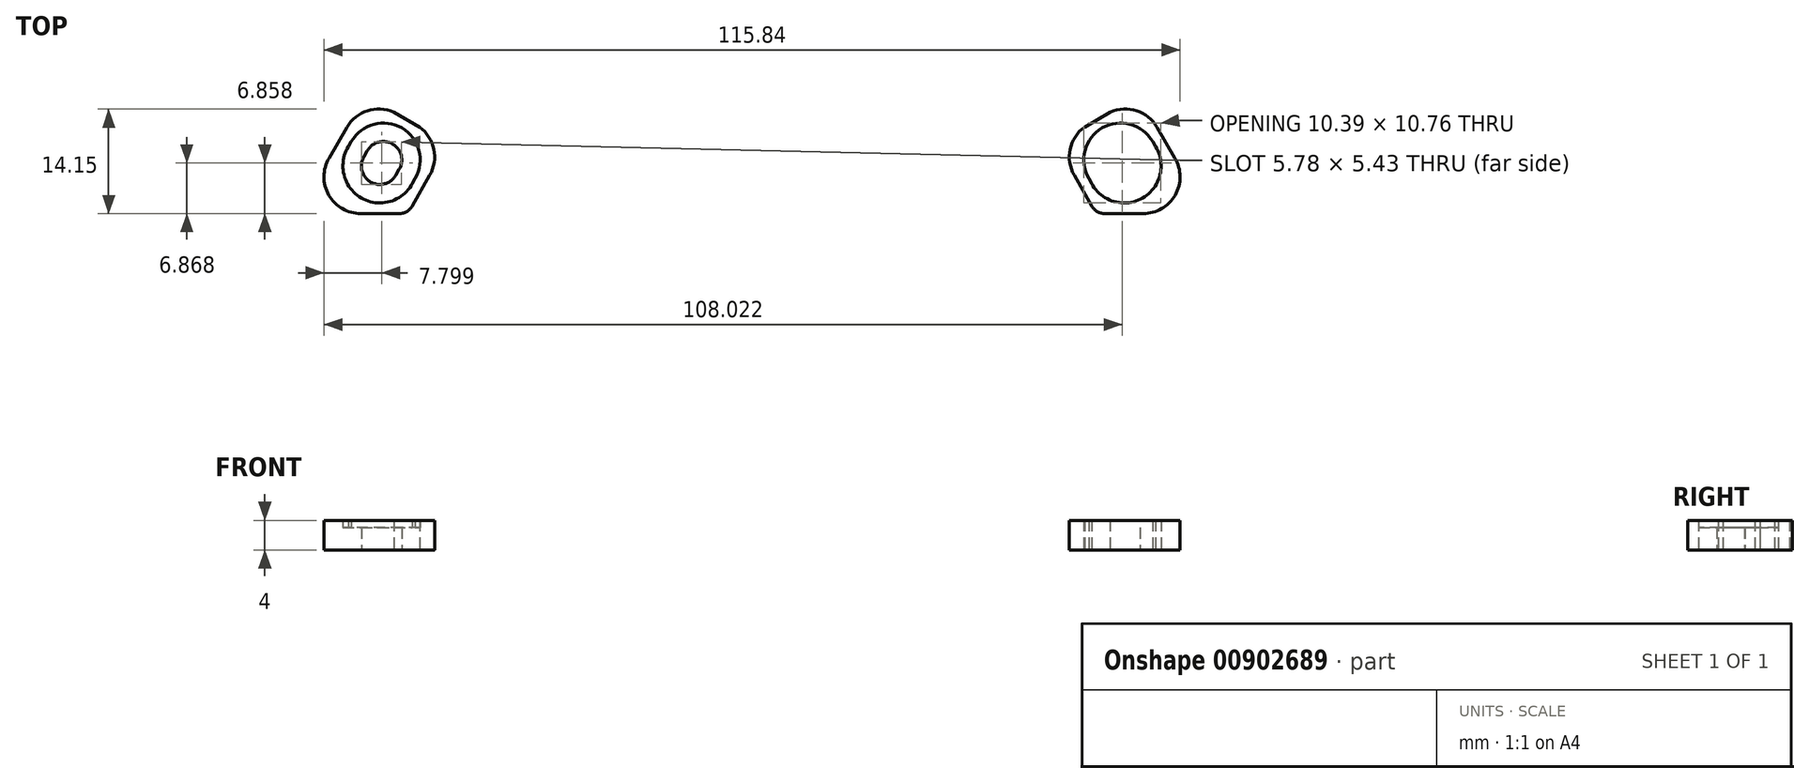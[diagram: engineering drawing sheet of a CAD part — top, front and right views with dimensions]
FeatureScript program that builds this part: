
annotation { "Feature Type Name" : "Feature", "Feature Type Description" : "" }
export const myFeature = defineFeature(function(context is Context, id is Id, definition is map)
    precondition{}
    {
        {
            var Q0;
            Q0=qCreatedBy(makeId("Top.planeOp"),FACE);
            var sketch = newSketch(context, id + "F0", { "sketchPlane" : qUnion([Q0])});
            skArc(sketch, "E0", {"start": v(-48.48, -109.77) * mm, "mid": v(-24.77, -117.42) * mm, "end": v(0, -120) * mm});
            skLineSegment(sketch, "E1", {"start": v(0, -120) * mm, "end": v(0, -123.5) * mm, "construction": true});
            skLineSegment(sketch, "E2", {"start": v(0, -123.5) * mm, "end": v(-52.92, -123.5) * mm});
            skLineSegment(sketch, "E3", {"start": v(-52.92, -123.5) * mm, "end": v(-47.73, -123.5) * mm});
            skLineSegment(sketch, "E4", {"start": v(-57.24, -115.98) * mm, "end": v(-54.82, -111.82) * mm});
            skLineSegment(sketch, "E5", {"start": v(0, -120) * mm, "end": v(0, -95) * mm, "construction": true});
            skArc(sketch, "E6", {"start": v(-45.57, -118.73) * mm, "mid": v(-45.06, -114.94) * mm, "end": v(-47.38, -111.9) * mm});
            skArc(sketch, "E7", {"start": v(-51.6, -119.22) * mm, "mid": v(-49.7, -119.47) * mm, "end": v(-48.19, -118.3) * mm});
            skArc(sketch, "E8", {"start": v(-47.73, -117.5) * mm, "mid": v(-47.47, -115.6) * mm, "end": v(-48.63, -114.07) * mm});
            skLineSegment(sketch, "E9", {"start": v(-47.73, -117.5) * mm, "end": v(-48.2, -118.31) * mm});
            skArc(sketch, "E10", {"start": v(-52.86, -121.38) * mm, "mid": v(-49, -121.86) * mm, "end": v(-45.95, -119.42) * mm});
            skLineSegment(sketch, "E11", {"start": v(-45.57, -118.73) * mm, "end": v(-45.95, -119.42) * mm});
            skPoint(sketch, "E12.orphan", {"position": v(-50.12, -116.64) * mm});
            skArc(sketch, "E13.MirrorCS", {"start": v(-52.05, -115) * mm, "mid": v(-50.54, -113.82) * mm, "end": v(-48.63, -114.07) * mm});
            skArc(sketch, "E14.MirrorCS", {"start": v(-54.2, -113.74) * mm, "mid": v(-51.17, -111.41) * mm, "end": v(-47.38, -111.9) * mm});
            skArc(sketch, "E15.MirrorCS", {"start": v(-51.6, -119.22) * mm, "mid": v(-52.77, -117.7) * mm, "end": v(-52.52, -115.8) * mm});
            skLineSegment(sketch, "E16.MirrorCS", {"start": v(-52.05, -115) * mm, "end": v(-52.53, -115.81) * mm});
            skLineSegment(sketch, "E17.MirrorCS", {"start": v(-54.2, -113.74) * mm, "end": v(-54.6, -114.42) * mm});
            skArc(sketch, "E18.MirrorCS", {"start": v(-52.86, -121.38) * mm, "mid": v(-55.2, -118.27) * mm, "end": v(-54.6, -114.42) * mm});
            skPoint(sketch, "E19.visualSharp", {"position": v(-61.63, -123.5) * mm});
            skArc(sketch, "E19.filletArc", {"start": v(-57.24, -115.98) * mm, "mid": v(-57.26, -120.99) * mm, "end": v(-52.92, -123.5) * mm});
            skPoint(sketch, "E20.visualSharp", {"position": v(-52.52, -107.9) * mm});
            skArc(sketch, "E20.filletArc", {"start": v(-48.48, -109.77) * mm, "mid": v(-52.04, -109.59) * mm, "end": v(-54.82, -111.82) * mm});
            skLineSegment(sketch, "E21", {"start": v(0, -95) * mm, "end": v(0, -95) * mm});
            skLineSegment(sketch, "E22", {"start": v(-7.5, -102.5) * mm, "end": v(-7.5, -119.77) * mm});
            skPoint(sketch, "E23.visualSharp", {"position": v(-7.5, -95) * mm});
            skArc(sketch, "E23.filletArc", {"start": v(0, -95) * mm, "mid": v(-5.3, -97.2) * mm, "end": v(-7.5, -102.5) * mm});
            skLineSegment(sketch, "E24", {"start": v(-49.88, -116.23) * mm, "end": v(-50.36, -117.05) * mm, "construction": true});
            skLineSegment(sketch, "E25.MirrorCS", {"start": v(-46, -122.48) * mm, "end": v(-43.6, -118.3) * mm});
            skArc(sketch, "E26.MirrorCS", {"start": v(-44.99, -111.79) * mm, "mid": v(-43.05, -114.78) * mm, "end": v(-43.6, -118.3) * mm});
            skPoint(sketch, "E27.trimOffspring.end.orphan", {"position": v(-54.66, -122.5) * mm});
            skPoint(sketch, "E28.orphan", {"position": v(-78.06, -74.9) * mm});
            skLineSegment(sketch, "E29.trimOffspring", {"start": v(-54.01, -123.38) * mm, "end": v(-55.93, -126.69) * mm, "construction": true});
            skPoint(sketch, "E30.MirrorCS.start.orphan", {"position": v(-44.99, -111.79) * mm});
            skLineSegment(sketch, "E31", {"start": v(-48.48, -109.77) * mm, "end": v(-44.99, -111.79) * mm});
            skPoint(sketch, "E32.MirrorCS.start.orphan", {"position": v(-46, -122.48) * mm});
            skLineSegment(sketch, "E33", {"start": v(-44.28, -119.5) * mm, "end": v(-46, -122.5) * mm});
            skPoint(sketch, "E34.newPointA", {"position": v(0, -123.5) * mm});
            skArc(sketch, "E34.filletArc", {"start": v(-47.73, -123.5) * mm, "mid": v(-46.73, -123.23) * mm, "end": v(-46, -122.5) * mm});
            skLineSegment(sketch, "E35.MirrorCS", {"start": v(49.88, -116.23) * mm, "end": v(50.36, -117.05) * mm, "construction": true});
            skLineSegment(sketch, "E36.MirrorCS", {"start": v(48.48, -109.77) * mm, "end": v(44.99, -111.79) * mm});
            skLineSegment(sketch, "E37.MirrorCS", {"start": v(52.05, -115) * mm, "end": v(52.53, -115.81) * mm});
            skArc(sketch, "E38.MirrorCS", {"start": v(51.6, -119.22) * mm, "mid": v(49.7, -119.47) * mm, "end": v(48.19, -118.3) * mm});
            skArc(sketch, "E39.MirrorCS", {"start": v(51.6, -119.22) * mm, "mid": v(52.77, -117.7) * mm, "end": v(52.52, -115.8) * mm});
            skLineSegment(sketch, "E40.MirrorCS", {"start": v(46, -122.48) * mm, "end": v(43.6, -118.3) * mm});
            skLineSegment(sketch, "E41.MirrorCS", {"start": v(47.73, -117.5) * mm, "end": v(48.2, -118.31) * mm});
            skLineSegment(sketch, "E42.MirrorCS", {"start": v(45.57, -118.73) * mm, "end": v(45.95, -119.42) * mm});
            skLineSegment(sketch, "E43.MirrorCS", {"start": v(44.28, -119.5) * mm, "end": v(46, -122.5) * mm});
            skArc(sketch, "E44.MirrorCS", {"start": v(47.73, -117.5) * mm, "mid": v(47.47, -115.6) * mm, "end": v(48.63, -114.07) * mm});
            skArc(sketch, "E45.MirrorCS", {"start": v(47.73, -123.5) * mm, "mid": v(46.73, -123.23) * mm, "end": v(46, -122.5) * mm});
            skLineSegment(sketch, "E46.MirrorCS", {"start": v(54.2, -113.74) * mm, "end": v(54.6, -114.42) * mm});
            skArc(sketch, "E47.MirrorCS", {"start": v(52.05, -115) * mm, "mid": v(50.54, -113.82) * mm, "end": v(48.63, -114.07) * mm});
            skLineSegment(sketch, "E48.MirrorCS", {"start": v(54.01, -123.38) * mm, "end": v(55.93, -126.69) * mm, "construction": true});
            skPoint(sketch, "E49.MirrorP", {"position": v(54.66, -122.5) * mm});
            skArc(sketch, "E50.MirrorCS", {"start": v(48.48, -109.77) * mm, "mid": v(52.04, -109.59) * mm, "end": v(54.82, -111.82) * mm});
            skPoint(sketch, "E51.MirrorP", {"position": v(46, -122.48) * mm});
            skPoint(sketch, "E52.MirrorP", {"position": v(50.12, -116.64) * mm});
            skArc(sketch, "E53.MirrorCS", {"start": v(0, -95) * mm, "mid": v(5.3, -97.2) * mm, "end": v(7.5, -102.5) * mm});
            skPoint(sketch, "E54.MirrorP", {"position": v(7.5, -95) * mm});
            skPoint(sketch, "E55.MirrorP", {"position": v(44.99, -111.79) * mm});
            skArc(sketch, "E56.MirrorCS", {"start": v(48.48, -109.77) * mm, "mid": v(24.77, -117.42) * mm, "end": v(0, -120) * mm});
            skArc(sketch, "E57.MirrorCS", {"start": v(52.86, -121.38) * mm, "mid": v(49, -121.86) * mm, "end": v(45.95, -119.42) * mm});
            skPoint(sketch, "E58.MirrorP", {"position": v(61.63, -123.5) * mm});
            skArc(sketch, "E59.MirrorCS", {"start": v(57.24, -115.98) * mm, "mid": v(57.26, -120.99) * mm, "end": v(52.92, -123.5) * mm});
            skLineSegment(sketch, "E60.MirrorCS", {"start": v(0, -123.5) * mm, "end": v(52.92, -123.5) * mm});
            skLineSegment(sketch, "E61.MirrorCS", {"start": v(52.92, -123.5) * mm, "end": v(47.73, -123.5) * mm});
            skArc(sketch, "E62.MirrorCS", {"start": v(45.57, -118.73) * mm, "mid": v(45.06, -114.94) * mm, "end": v(47.38, -111.9) * mm});
            skPoint(sketch, "E63.MirrorP", {"position": v(52.52, -107.9) * mm});
            skArc(sketch, "E64.MirrorCS", {"start": v(52.86, -121.38) * mm, "mid": v(55.2, -118.27) * mm, "end": v(54.6, -114.42) * mm});
            skArc(sketch, "E65.MirrorCS", {"start": v(44.99, -111.79) * mm, "mid": v(43.05, -114.78) * mm, "end": v(43.6, -118.3) * mm});
            skLineSegment(sketch, "E66.MirrorCS", {"start": v(7.5, -102.5) * mm, "end": v(7.5, -119.77) * mm});
            skLineSegment(sketch, "E67.MirrorCS", {"start": v(57.24, -115.98) * mm, "end": v(54.82, -111.82) * mm});
            skArc(sketch, "E68.MirrorCS", {"start": v(54.2, -113.74) * mm, "mid": v(51.17, -111.41) * mm, "end": v(47.38, -111.9) * mm});
            skSolve(sketch);
        }
        {
            var Q0;
            Q0=makeQuery(id+"F0.imprint","IMPRINT",FACE,{"disambiguationData":[TD([[makeQuery(id+"F0.imprint","IMPRINT",EDGE,{"derivedFrom":sQuery(id+"F0.wireOp",EDGE,"E6")}),1.0]])]});
            var Q1;
            {var subQ4=sQuery(id+"F0.wireOp",EDGE,"E37.MirrorCS");Q1=makeQuery(id+"F0.imprint","IMPRINT",FACE,{"disambiguationData":[TD([[makeQuery(id+"F0.imprint","IMPRINT",EDGE,{"derivedFrom":subQ4}),1.0]])]});}
            extrude(context, id + "F1", {"entities" : qUnion([Q0, Q1]), "depth" : 3 * mm, "offsetDistance" : 25 * mm});
        }
        {
            var Q0;
            Q0=makeQuery(id+"F0.imprint","IMPRINT",FACE,{"disambiguationData":[TD([[makeQuery(id+"F0.imprint","IMPRINT",EDGE,{"derivedFrom":sQuery(id+"F0.wireOp",EDGE,"E3")}),1.0]])]});
            var Q1;
            Q1=makeQuery(id+"F0.imprint","IMPRINT",FACE,{"disambiguationData":[TD([[makeQuery(id+"F0.imprint","IMPRINT",EDGE,{"derivedFrom":sQuery(id+"F0.wireOp",EDGE,"E36.MirrorCS")}),1.0]])]});
            extrude(context, id + "F2", {"entities" : qUnion([Q0, Q1]), "operationType" : NewBodyOperationType.ADD, "depth" : 4 * mm, "offsetDistance" : 25 * mm});
        }
        {
            var Q0;
            Q0=makeQuery(id+"F0.imprint","IMPRINT",FACE,{"disambiguationData":[TD([[makeQuery(id+"F0.imprint","IMPRINT",EDGE,{"derivedFrom":sQuery(id+"F0.wireOp",EDGE,"E2")}),-1.0]])]});
            extrude(context, id + "F3", {"entities" : qUnion([Q0]), "operationType" : NewBodyOperationType.ADD, "depth" : 4 * mm, "offsetDistance" : 25 * mm});
        }
    });
